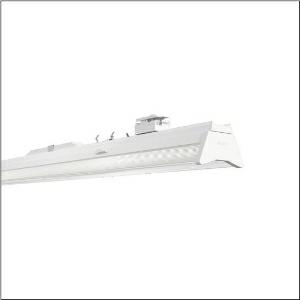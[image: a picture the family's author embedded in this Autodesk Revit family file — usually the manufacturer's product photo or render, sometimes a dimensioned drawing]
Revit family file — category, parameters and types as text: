
# Revit family: licross_r__11_performance_ho_51td16dn6exm_746f
name_source: partatom
category: Lighting Fixtures
units: mm (PartAtom-declared; Revit-internal decimal feet)

## family parameters
Cut with Voids When Loaded = No
Host = Face
Light Source = No
Part Type = Normal
Room Calculation Point = No
Round Connector Dimension = Use Diameter
Shared = No

## types (1)
- --- (1 x LED, 14180 lm, 81.4 W, 6500K)
    Apparent Load = 81 VA
    CIE Flux Codes = 63 87 95 78 100
    Color Rendering = 80
    Color Temperature = 6500K
    Default Elevation = 1800 mm
    Description = Licross® 11 Performance HO, luminaire insert, of sheet steel, galvanised, coil coated, white, length: 1.500mm, width: 120mm, height: 123mm, LED rated luminous flux: 14.180lm, light colour: 865, control gear: DALI 2, with plug, 5-pole, with phase selection, mains connection: 220..240V, AC, 50/60Hz, rated input power: 81W, halogen-free wiring, primary light control with lens, of plastic, primary optical cover: cover, of PMMA, light emission: direct/indirect distribution, primary light characteristic: symmetric, protection rating (complete): IP54, insulation class (complete): insulation class I (protective earthing), certification: CE, ENEC, VDE, UKCA, protection symbol: D if used in an environment with non-conductive dust loads with corresponding accessories, impact resistance: IK06, permissible ambient temperature for indoor applications: -25..+35°C, corresponds to IFS (International Featured Standards) requirements for safety and quality in the food industry, reducing of maximum allowable ambient temperature of 5°C with ceiling mounting, LABS conformity tested according to VDMA 24364:2018-05, packaging unit: 1 piece
    Height = 114 mm
    Lamp = 1 x LED
    Lamp Light Flux = 14180 lm
    Lamp Power = 81.4 W
    Lamp count = 1
    Length = 1500 mm
    Luminous efficacy = 174 lm/W
    Manufacturer = Siteco
    ModVariant = No
    Model = 51TD16DN6EXM
    Mounting Place = Ceiling
    Mounting Type = Pendant
    Number of Poles = 1
    OnlyDefault = Yes
    Power Factor = 1
    Product Name = Licross® 11 Performance HO
    Product group = luminaire insert
    ProductGroupID = 902
    Protection Class = Protection class I
    Protection Degree = IP 54
    RLX_Detail_Level = 1
    RLX_Emergency_Light_Flux = 0 lm
    RLX_Emergency_Type = 0
    RLX_Emergency_Type_DB = No
    RlxData = <blob elided: 34065 chars, md5=de791b19>
    Socket = socket
    Standby Power = 0 W
    System Light Flux = 14180 lm
    System Power = 81 W
    Type Comments = factory setting: luminous flux: 100 % | dim-lin: 254 | 550 mA
    Type Image = l_1256138.jpg
    URL = http://relux.com
    VarID = @adj_068316
    Voltage = 0 V
    Weight = 0.00 kg
    Width = 120 mm

## geometry (parser evidence)
native form markers: Blend x4, Sweep x12
no freeform markers — native parametric forms only
